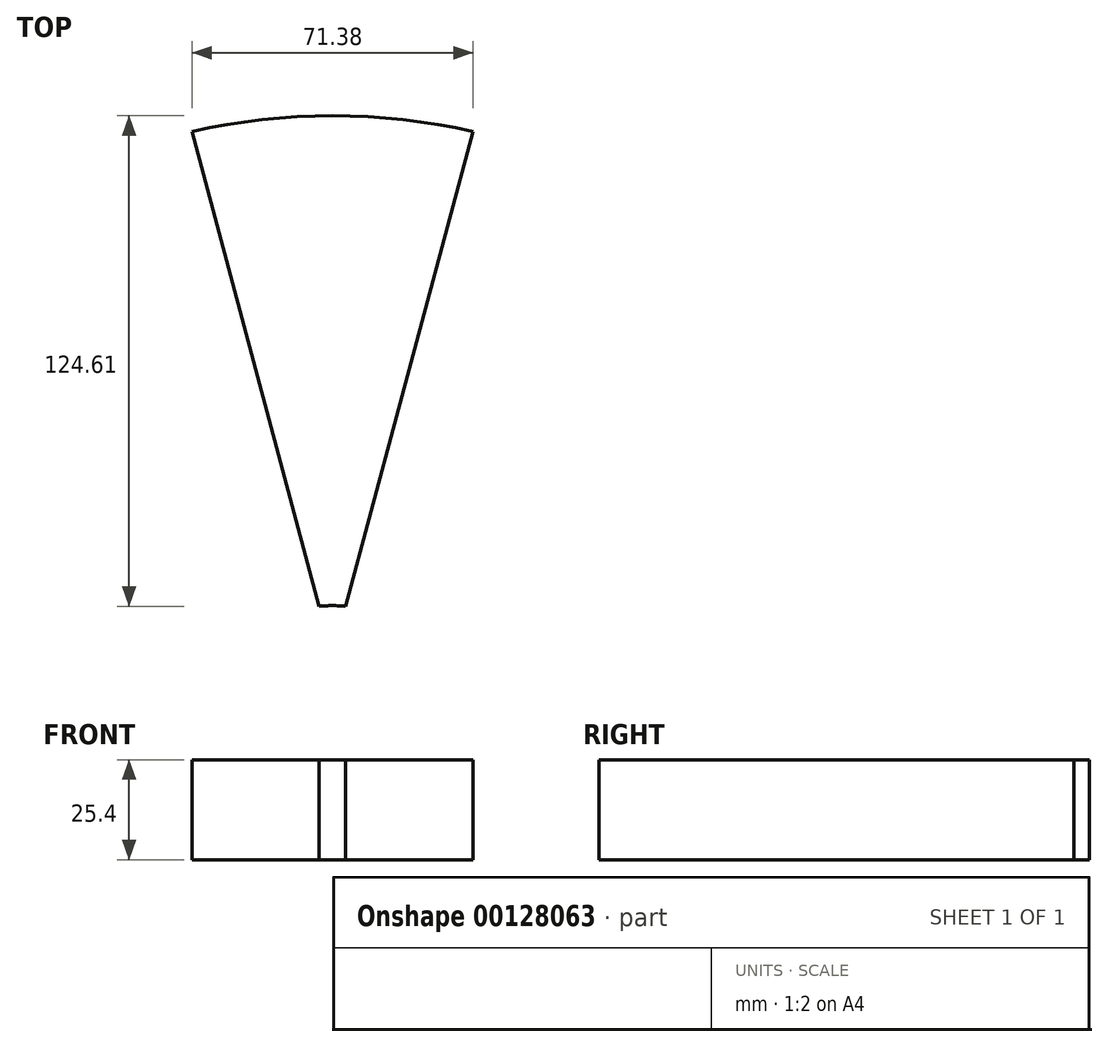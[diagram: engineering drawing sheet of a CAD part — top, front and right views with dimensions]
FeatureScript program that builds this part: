
annotation { "Feature Type Name" : "Feature", "Feature Type Description" : "" }
export const myFeature = defineFeature(function(context is Context, id is Id, definition is map)
    precondition{}
    {
        {
            var Q0;
            Q0=qCreatedBy(makeId("Top.planeOp"),FACE);
            var sketch = newSketch(context, id + "F0", { "sketchPlane" : qUnion([Q0])});
            skArc(sketch, "E0", {"start": v(43.5, 163.21) * mm, "mid": v(0, 168.91) * mm, "end": v(-43.5, 163.21) * mm, "construction": true});
            skArc(sketch, "E1", {"start": v(8, 30.73) * mm, "mid": v(0, 31.75) * mm, "end": v(-8, 30.73) * mm, "construction": true});
            skLineSegment(sketch, "E2", {"start": v(8, 30.73) * mm, "end": v(43.5, 163.21) * mm, "construction": true});
            skLineSegment(sketch, "E3", {"start": v(-43.5, 163.21) * mm, "end": v(-8, 30.73) * mm, "construction": true});
            skLineSegment(sketch, "E4", {"start": v(0, 0) * mm, "end": v(0, 184.5) * mm});
            skArc(sketch, "E5", {"start": v(35.69, 158.6) * mm, "mid": v(0, 162.56) * mm, "end": v(-35.69, 158.6) * mm});
            skLineSegment(sketch, "E6", {"start": v(3.36, 37.95) * mm, "end": v(35.69, 158.6) * mm});
            skLineSegment(sketch, "E7", {"start": v(-35.69, 158.6) * mm, "end": v(-3.36, 37.95) * mm});
            skArc(sketch, "E8", {"start": v(3.36, 37.95) * mm, "mid": v(0, 38.1) * mm, "end": v(-3.36, 37.95) * mm});
            skSolve(sketch);
        }
        {
            var Q0;
            Q0 = qSketchRegion(id + "F0", true);
            extrude(context, id + "F1", {"entities" : qUnion([Q0]), "depth" : 25.4 * mm});
        }
    });
